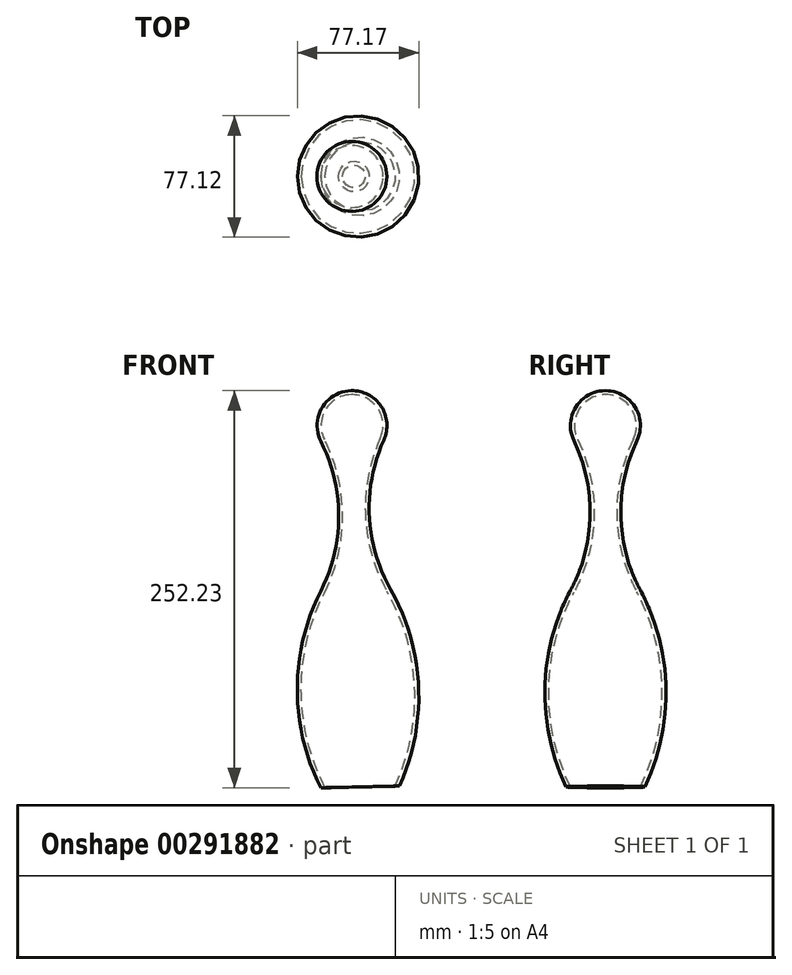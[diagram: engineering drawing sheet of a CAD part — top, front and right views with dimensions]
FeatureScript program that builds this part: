
annotation { "Feature Type Name" : "Feature", "Feature Type Description" : "" }
export const myFeature = defineFeature(function(context is Context, id is Id, definition is map)
    precondition{}
    {
        {
            var Q0;
            Q0=qCreatedBy(makeId("Front.planeOp"),FACE);
            var sketch = newSketch(context, id + "F0", { "sketchPlane" : qUnion([Q0])});
            skLineSegment(sketch, "E0", {"start": v(0, 0) * mm, "end": v(-25, 0) * mm});
            skArc(sketch, "E1", {"start": v(-25, 125) * mm, "mid": v(-39.95, 62.5) * mm, "end": v(-25, 0) * mm});
            skArc(sketch, "E2", {"start": v(-25, 125) * mm, "mid": v(-13.64, 172.5) * mm, "end": v(-25, 220) * mm});
            skArc(sketch, "E3", {"start": v(-5.71, 252.22) * mm, "mid": v(-24.25, 241.43) * mm, "end": v(-25, 220) * mm});
            skLineSegment(sketch, "E4", {"start": v(0, 0) * mm, "end": v(-5.71, 252.22) * mm});
            skSolve(sketch);
        }
        {
            var Q0;
            Q0=makeQuery(id+"F0.imprint","IMPRINT",FACE,{"disambiguationData":[TD([[makeQuery(id+"F0.imprint","IMPRINT",EDGE,{"derivedFrom":sQuery(id+"F0.wireOp",EDGE,"E0")}),-1.0]])]});
            var Q1;
            Q1=sQuery(id+"F0.wireOp",EDGE,"E3");
            var Q2;
            Q2=sQuery(id+"F0.wireOp",EDGE,"E2");
            var Q3;
            Q3=sQuery(id+"F0.wireOp",EDGE,"E1");
            var Q4;
            Q4=sQuery(id+"F0.wireOp",EDGE,"E0");
            var Q5;
            Q5=sQuery(id+"F0.wireOp",EDGE,"E4");
            revolve(context, id + "F1", {"entities" : qUnion([Q0]), "surfaceEntities" : qUnion([Q1, Q2, Q3, Q4]), "axis" : qUnion([Q5]), "revolveType" : RevolveType.FULL});
        }
        {
            var Q0;
            Q0=makeQuery(id+"F1.opRevolve","SWEPT_FACE",FACE,{"disambiguationData":[OSD([sQuery(id+"F0.wireOp",EDGE,"E0")])]});
            shell(context, id + "F2", {"entities" : qUnion([Q0]), "thickness" : 2.5 * mm});
        }
    });
